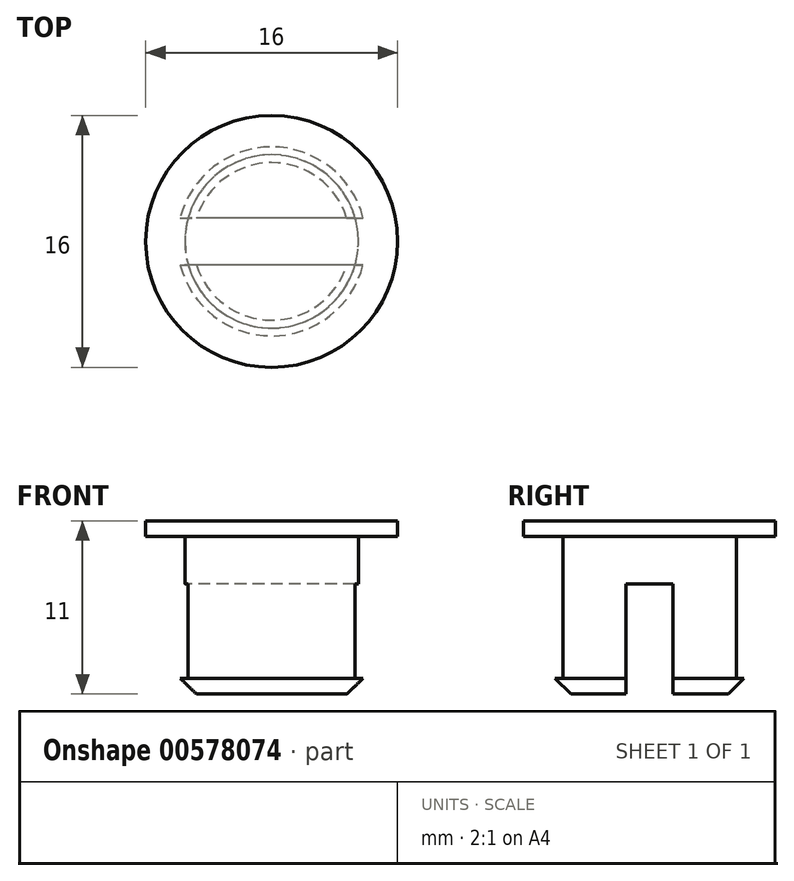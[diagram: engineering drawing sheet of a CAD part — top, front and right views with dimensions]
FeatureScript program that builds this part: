
annotation { "Feature Type Name" : "Feature", "Feature Type Description" : "" }
export const myFeature = defineFeature(function(context is Context, id is Id, definition is map)
    precondition{}
    {
        {
            var Q0;
            Q0=qCreatedBy(makeId("Top.planeOp"),FACE);
            var sketch = newSketch(context, id + "F0", { "sketchPlane" : qUnion([Q0])});
            skCircle(sketch, "E0", {"center": v(0, 0) * mm, "radius": 8 * mm});
            skSolve(sketch);
        }
        {
            var Q0;
            Q0=makeQuery(id+"F0.imprint","IMPRINT",FACE,{"disambiguationData":[TD([[makeQuery(id+"F0.imprint","IMPRINT",EDGE,{"derivedFrom":sQuery(id+"F0.wireOp",EDGE,"E0")}),1.0]])]});
            extrude(context, id + "F1", {"entities" : qUnion([Q0]), "depth" : 1 * mm, "offsetDistance" : 25 * mm});
        }
        {
            var Q0;
            Q0=makeQuery(id+"F1.opExtrude","CAP_FACE",FACE,{"disambiguationData":[OSD([sQuery(id+"F0.wireOp",EDGE,"E0")])],"isStart":true});
            var sketch = newSketch(context, id + "F2", { "sketchPlane" : qUnion([Q0])});
            skCircle(sketch, "E1", {"center": v(0, 0) * mm, "radius": 6 * mm});
            skSolve(sketch);
        }
        {
            var Q0;
            Q0=makeQuery(id+"F2.imprint","IMPRINT",FACE,{"disambiguationData":[TD([[makeQuery(id+"F2.imprint","IMPRINT",EDGE,{"derivedFrom":sQuery(id+"F2.wireOp",EDGE,"E1")}),1.0]])]});
            extrude(context, id + "F3", {"entities" : qUnion([Q0]), "operationType" : NewBodyOperationType.ADD, "depth" : 10 * mm, "offsetDistance" : 25 * mm});
        }
        {
            var Q0;
            Q0=makeQuery(id+"F3.opExtrude","CAP_FACE",FACE,{"disambiguationData":[OSD([sQuery(id+"F2.wireOp",EDGE,"E1")])],"isStart":false});
            var sketch = newSketch(context, id + "F4", { "sketchPlane" : qUnion([Q0])});
            skCircle(sketch, "E2", {"center": v(0, 0) * mm, "radius": 6 * mm});
            skLineSegment(sketch, "E3", {"start": v(5.8, 1.5) * mm, "end": v(-5.8, 1.5) * mm});
            skLineSegment(sketch, "E4", {"start": v(5.8, -1.5) * mm, "end": v(-5.8, -1.5) * mm});
            skSolve(sketch);
        }
        {
            var Q0;
            {var subQ0=sQuery(id+"F4.wireOp",EDGE,"E3");Q0=makeQuery(id+"F4.imprint","IMPRINT",FACE,{"disambiguationData":[TD([[makeQuery(id+"F4.imprint","IMPRINT",EDGE,{"derivedFrom":subQ0}),1.0]])]});}
            extrude(context, id + "F5", {"entities" : qUnion([Q0]), "operationType" : NewBodyOperationType.REMOVE, "oppositeDirection" : true, "depth" : 7 * mm, "offsetDistance" : 25 * mm});
        }
        {
            var Q0;
            {var subQ0=sQuery(id+"F2.wireOp",EDGE,"E1");Q0=makeQuery(id+"F5.boolean.opBoolean","SPLIT",EDGE,{"disambiguationData":[TD([makeQuery(id+"F5.opExtrude","SWEPT_FACE",FACE,{"disambiguationData":[OSD([sQuery(id+"F4.wireOp",EDGE,"E4")])]})])],"derivedFrom":makeQuery(id+"F3.opExtrude","CAP_EDGE",EDGE,{"disambiguationData":[OSD([subQ0])],"isStart":false})});}
            var Q1;
            {var subQ0=sQuery(id+"F2.wireOp",EDGE,"E1");Q1=makeQuery(id+"F5.boolean.opBoolean","SPLIT",EDGE,{"disambiguationData":[TD([makeQuery(id+"F5.opExtrude","SWEPT_FACE",FACE,{"disambiguationData":[OSD([sQuery(id+"F4.wireOp",EDGE,"E3")])]})])],"derivedFrom":makeQuery(id+"F3.opExtrude","CAP_EDGE",EDGE,{"disambiguationData":[OSD([subQ0])],"isStart":false})});}
            chamfer(context, id + "F6", {"entities" : qUnion([Q0, Q1]), "width" : 1 * mm, "tangentPropagation" : true});
        }
        {
            var Q0;
            {var subQ0=sQuery(id+"F2.wireOp",EDGE,"E1");Q0=makeQuery(id+"F5.boolean.opBoolean","SPLIT",FACE,{"disambiguationData":[TD([makeQuery(id+"F5.opExtrude","SWEPT_FACE",FACE,{"disambiguationData":[OSD([sQuery(id+"F4.wireOp",EDGE,"E3")])]})])],"derivedFrom":makeQuery(id+"F3.opExtrude","CAP_FACE",FACE,{"disambiguationData":[OSD([subQ0])],"isStart":false})});}
            cPlane(context, id + "F7", {"entities" : qUnion([Q0]), "cplaneType" : CPlaneType.OFFSET, "offset" : 1 * mm, "oppositeDirection" : true, "width" : 150 * mm, "height" : 150 * mm});
        }
        {
            var Q0;
            Q0=qCreatedBy(id+"F7.planeOp",FACE);
            var sketch = newSketch(context, id + "F8", { "sketchPlane" : qUnion([Q0])});
            skCircle(sketch, "E5", {"center": v(0, 0) * mm, "radius": 6 * mm});
            skCircle(sketch, "E6", {"center": v(0, 0) * mm, "radius": 5.5 * mm});
            skCircle(sketch, "E7", {"center": v(0, 0) * mm, "radius": 5 * mm});
            skSolve(sketch);
        }
        {
            var Q0;
            Q0 = qSketchRegion(id + "F8", true);
            var Q1;
            Q1=makeQuery(id+"F8.imprint","IMPRINT",FACE,{"disambiguationData":[TD([[makeQuery(id+"F8.imprint","IMPRINT",EDGE,{"derivedFrom":sQuery(id+"F8.wireOp",EDGE,"E5")}),1.0]])]});
            extrude(context, id + "F9", {"entities" : qUnion([Q0, Q1]), "operationType" : NewBodyOperationType.REMOVE, "oppositeDirection" : true, "depth" : 9 * mm, "offsetDistance" : 25 * mm});
        }
    });
